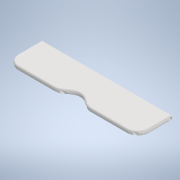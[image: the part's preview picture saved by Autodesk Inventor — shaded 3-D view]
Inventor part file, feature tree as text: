
AUTODESK INVENTOR PART (.ipt)
format: ipt  version: 2020.3 (Build 243373000, 373)  size: 279,552 bytes
history: native  units: mm
features: sketch x5, extrude x4, fillet x2, chamfer x1
ambient origin geometry x8: Origin, YZ Plane, XZ Plane, XY Plane, X Axis, Y Axis, Z Axis, Center Point
bodies: Solid1 (feature_tree)
feature tree (12):
  extrude  "Extrusion1"  Depth=35.0mm
  extrude  "Extrusion2"  Depth=2.5mm
  extrude  "Extrusion3"  TaperAngle=0.0deg  [1 undecoded]
  sketch  "Sketch4"  dims[d8=30.0mm d9=10.0mm d10=0.0mm d11=0.0mm d12=2.5mm]
  extrude  "Extrusion4"  Depth=10.0mm
  fillet  "Fillet1"  [1 undecoded]
  fillet  "Fillet2"  Radius=2.5mm
  chamfer  "Chamfer1"  [1 undecoded]
  sketch  "Sketch1"  dims[d0=130.0mm d1=35.0mm]
  sketch  "Sketch2"  dims[d2=4.0mm d3=0.0mm d4=2.5mm]
  sketch  "Sketch3"  dims[d5=2.5mm d6=0.0mm d7=0.0mm]
  sketch  "Sketch5"  dims[d13=2.5mm d14=0.0mm d15=0.0mm d16=11.5mm d17=1.75mm d18=1.0mm d19=2.0mm d20=45.0deg]
note: 3 required parameter values undecoded (feature->parameter linkage not recoverable at this tier; creation-order binding heuristic only, values carry confidence <= 0.55)
